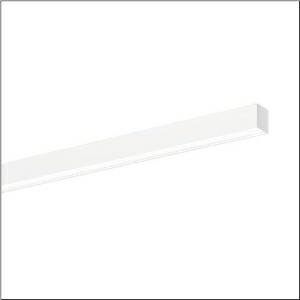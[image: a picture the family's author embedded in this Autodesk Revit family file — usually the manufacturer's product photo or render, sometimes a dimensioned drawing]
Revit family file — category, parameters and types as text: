
# Revit family: silica_r__21_51mx20dc35wb_3ec9
name_source: partatom
category: Lighting Fixtures
units: mm (PartAtom-declared; Revit-internal decimal feet)

## family parameters
Cut with Voids When Loaded = No
Host = Face
Light Source = No
Part Type = Normal
Room Calculation Point = No
Round Connector Dimension = Use Diameter
Shared = No

## types (1)
- --- (1 x LED, 6000 lm, 42.6 W, 3000K)
    Apparent Load = 43 VA
    CIE Flux Codes = 48 79 96 100 100
    Color Rendering = 80
    Color Temperature = 3000K
    Default Elevation = 1800 mm
    Description = Silica® 21, office luminaire, primary optical cover: cover, of PMMA, opal, light emission: direct distribution, primary light characteristic: symmetric, installation type: surface-mounted, LED, rated luminous flux: 6.000lm, luminous efficacy: 141lm/W, light colour: 830, colour temperature: 3000K, control gear: DALI 2, with terminal, 3+2-pole, max. 2.5mm², mains connection: 220..240V, AC, 50/60Hz, rated input power: 42.6W, luminaire housing, of aluminium, traffic white (RAL 9016), length: 3.004mm, width: 53mm, height: 53mm, protection rating (complete): IP20, insulation class (complete): insulation class I (protective earthing), certification: CE, permissible operating ambient temperature: 0..+35°C, standard: EN 50419, packaging unit: 1 piece
    Height = 53 mm
    Lamp = 1 x LED
    Lamp Light Flux = 6000 lm
    Lamp Power = 42.6 W
    Lamp count = 1
    Length = 3004 mm
    Luminous efficacy = 141 lm/W
    Manufacturer = Siteco
    ModVariant = No
    Model = 51MX20DC35WB
    Mounting Place = Ceiling
    Mounting Type = Surface mounted
    Number of Poles = 1
    OnlyDefault = Yes
    Power Factor = 1
    Product Name = Silica® 21
    Product group = office luminaire | ceiling mounted
    ProductGroupID = 302
    Protection Class = Protection class I
    Protection Degree = IP 20
    RLX_Detail_Level = 1
    RLX_Emergency_Light_Flux = 0 lm
    RLX_Emergency_Type = 0
    RLX_Emergency_Type_DB = No
    RlxData = <blob elided: 23873 chars, md5=79aebcbb>
    Socket = socket
    Standby Power = 0 W
    System Light Flux = 6000 lm
    System Power = 43 W
    Type Comments = factory setting: luminous flux: 100 % | dim-lin: 254 | 233 mA
    Type Image = l_1335877.jpg
    URL = http://relux.com
    VarID = @adj_117928
    Voltage = 0 V
    Weight = 0.00 kg
    Width = 53 mm

## geometry (parser evidence)
native form markers: Blend x4, Sweep x11
no freeform markers — native parametric forms only
